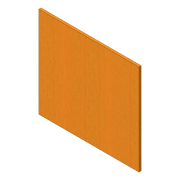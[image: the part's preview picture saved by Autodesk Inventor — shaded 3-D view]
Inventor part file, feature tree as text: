
AUTODESK INVENTOR PART (.ipt)
format: ipt  version: 2016 (Build 200138000, 138)  size: 89,600 bytes
history: native  units: in
note: dims shown in document units (in); Inventor stores cm internally (conversion verified against a paired STEP export)
features: extrude x1, sketch x1
ambient origin geometry x8: Origin, YZ Plane, XZ Plane, XY Plane, X Axis, Y Axis, Z Axis, Center Point
bodies: Solid1 (feature_tree)
feature tree (2):
  extrude  "Extrusion1"  Depth=20.0in
  sketch  "Sketch1"  dims[d0=22.0in d1=20.0in d2=0.5in d3=0.0in]
